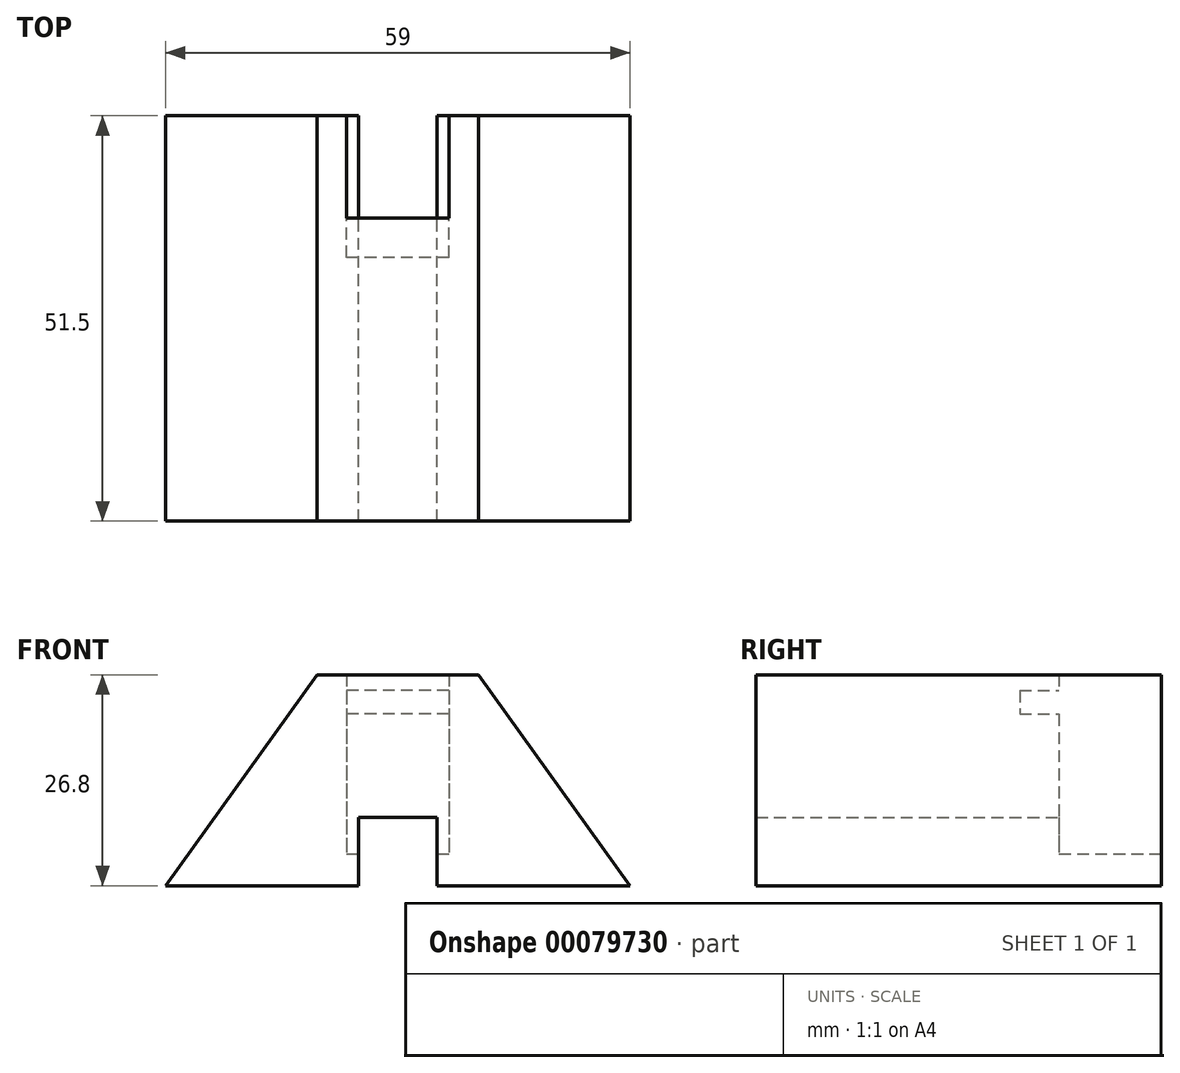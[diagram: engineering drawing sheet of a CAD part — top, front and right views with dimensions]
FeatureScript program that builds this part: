
annotation { "Feature Type Name" : "Feature", "Feature Type Description" : "" }
export const myFeature = defineFeature(function(context is Context, id is Id, definition is map)
    precondition{}
    {
        {
            var Q0;
            Q0=qCreatedBy(makeId("Top.planeOp"),FACE);
            var sketch = newSketch(context, id + "F0", { "sketchPlane" : qUnion([Q0])});
            skPoint(sketch, "E0.middle", {"position": v(0, 0) * mm});
            skLineSegment(sketch, "E1.bottom", {"start": v(-10.25, 25.75) * mm, "end": v(10.25, 25.75) * mm});
            skLineSegment(sketch, "E1.top", {"start": v(-10.25, -25.75) * mm, "end": v(10.25, -25.75) * mm});
            skLineSegment(sketch, "E1.left", {"start": v(-10.25, 25.75) * mm, "end": v(-10.25, -25.75) * mm});
            skLineSegment(sketch, "E1.right", {"start": v(10.25, 25.75) * mm, "end": v(10.25, -25.75) * mm});
            skLineSegment(sketch, "E2.bottom", {"start": v(-10.25, 25.75) * mm, "end": v(-29.5, 25.75) * mm});
            skLineSegment(sketch, "E2.top", {"start": v(-10.25, -25.75) * mm, "end": v(-29.5, -25.75) * mm});
            skLineSegment(sketch, "E2.right", {"start": v(-29.5, 25.75) * mm, "end": v(-29.5, -25.75) * mm});
            skLineSegment(sketch, "E3.bottom", {"start": v(10.25, 25.75) * mm, "end": v(29.5, 25.75) * mm});
            skLineSegment(sketch, "E3.top", {"start": v(10.25, -25.75) * mm, "end": v(29.5, -25.75) * mm});
            skLineSegment(sketch, "E3.right", {"start": v(29.5, 25.75) * mm, "end": v(29.5, -25.75) * mm});
            skSolve(sketch);
        }
        {
            var Q0;
            Q0 = qSketchRegion(id + "F0", true);
            extrude(context, id + "F1", {"entities" : qUnion([Q0]), "depth" : 26.8 * mm});
        }
        {
            var Q0;
            Q0=qCreatedBy(makeId("Top.planeOp"),FACE);
            var sketch = newSketch(context, id + "F2", { "sketchPlane" : qUnion([Q0])});
            skLineSegment(sketch, "E4.bottom", {"start": v(-6.5, 25.75) * mm, "end": v(6.5, 25.75) * mm});
            skLineSegment(sketch, "E4.top", {"start": v(-6.5, 12.75) * mm, "end": v(6.5, 12.75) * mm});
            skLineSegment(sketch, "E4.left", {"start": v(-6.5, 25.75) * mm, "end": v(-6.5, 12.75) * mm});
            skLineSegment(sketch, "E4.right", {"start": v(6.5, 25.75) * mm, "end": v(6.5, 12.75) * mm});
            skSolve(sketch);
        }
        {
            var Q0;
            Q0 = qSketchRegion(id + "F2", true);
            extrude(context, id + "F3", {"entities" : qUnion([Q0]), "operationType" : NewBodyOperationType.REMOVE, "depth" : 26.8 * mm});
        }
        {
            var Q0;
            Q0=makeQuery(id+"F0.imprint","IMPRINT",FACE,{"disambiguationData":[TD([[makeQuery(id+"F0.imprint","IMPRINT",EDGE,{"derivedFrom":sQuery(id+"F0.wireOp",EDGE,"E1.bottom")}),-1.0]])]});
            var sketch = newSketch(context, id + "F4", { "sketchPlane" : qUnion([Q0])});
            skLineSegment(sketch, "E5.bottom", {"start": v(-6.5, 12.75) * mm, "end": v(-5, 12.75) * mm});
            skLineSegment(sketch, "E5.top", {"start": v(-6.5, 25.75) * mm, "end": v(-5, 25.75) * mm});
            skLineSegment(sketch, "E5.left", {"start": v(-6.5, 12.75) * mm, "end": v(-6.5, 25.75) * mm});
            skLineSegment(sketch, "E5.right", {"start": v(-5, 12.75) * mm, "end": v(-5, 25.75) * mm});
            skLineSegment(sketch, "E6.bottom", {"start": v(5, 12.75) * mm, "end": v(6.5, 12.75) * mm});
            skLineSegment(sketch, "E6.top", {"start": v(5, 25.75) * mm, "end": v(6.5, 25.75) * mm});
            skLineSegment(sketch, "E6.left", {"start": v(5, 12.75) * mm, "end": v(5, 25.75) * mm});
            skLineSegment(sketch, "E6.right", {"start": v(6.5, 12.75) * mm, "end": v(6.5, 25.75) * mm});
            skSolve(sketch);
        }
        {
            var Q0;
            Q0 = qSketchRegion(id + "F4", true);
            extrude(context, id + "F5", {"entities" : qUnion([Q0]), "operationType" : NewBodyOperationType.ADD, "depth" : 4.05 * mm});
        }
        {
            var Q0;
            {var subQ0=sQuery(id+"F0.wireOp",EDGE,"E3.right");var subQ2=sQuery(id+"F0.wireOp",EDGE,"E3.bottom");var subQ5=sQuery(id+"F0.wireOp",EDGE,"E2.bottom");var subQ7=sQuery(id+"F0.wireOp",EDGE,"E1.bottom");Q0=makeQuery(id+"F5.boolean.opBoolean","MERGE",FACE,{"derivedFrom":[makeQuery(id+"F3.boolean.opBoolean","SPLIT",FACE,{"disambiguationData":[TD([makeQuery(id+"F1.opExtrude","SWEPT_FACE",FACE,{"disambiguationData":[OSD([subQ0])]})])],"derivedFrom":makeQuery(id+"F1.opExtrude","SWEPT_FACE",FACE,{"disambiguationData":[OSD([subQ7,subQ5,subQ2])]})}),makeQuery(id+"F5.opExtrude","SWEPT_FACE",FACE,{"disambiguationData":[OSD([sQuery(id+"F4.wireOp",EDGE,"E6.top")])]})]});}
            var sketch = newSketch(context, id + "F6", { "sketchPlane" : qUnion([Q0])});
            skLineSegment(sketch, "E7", {"start": v(29.5, 0) * mm, "end": v(10.24, 26.8) * mm});
            skLineSegment(sketch, "E8", {"start": v(10.24, 26.8) * mm, "end": v(29.5, 26.8) * mm});
            skLineSegment(sketch, "E9", {"start": v(29.5, 26.8) * mm, "end": v(29.5, 0) * mm});
            skLineSegment(sketch, "E10", {"start": v(-10.24, 26.8) * mm, "end": v(-29.5, 26.8) * mm});
            skLineSegment(sketch, "E11", {"start": v(-29.5, 26.8) * mm, "end": v(-29.5, 0) * mm});
            skLineSegment(sketch, "E12", {"start": v(-10.24, 26.8) * mm, "end": v(-29.5, 0) * mm});
            skSolve(sketch);
        }
        {
            var Q0;
            Q0 = qSketchRegion(id + "F6", true);
            extrude(context, id + "F7", {"entities" : qUnion([Q0]), "operationType" : NewBodyOperationType.REMOVE, "endBound" : BoundingType.THROUGH_ALL, "oppositeDirection" : true, "depth" : 25 * mm});
        }
        {
            var Q0;
            Q0=makeQuery(id+"F3.boolean.opBoolean","COPY",FACE,{"derivedFrom":makeQuery(id+"F3.opExtrude","SWEPT_FACE",FACE,{"disambiguationData":[OSD([sQuery(id+"F2.wireOp",EDGE,"E4.top")])]})});
            var sketch = newSketch(context, id + "F8", { "sketchPlane" : qUnion([Q0])});
            skLineSegment(sketch, "E13.bottom", {"start": v(-5, 8.67) * mm, "end": v(5, 8.67) * mm});
            skLineSegment(sketch, "E13.top", {"start": v(-5, 0) * mm, "end": v(5, 0) * mm});
            skLineSegment(sketch, "E13.left", {"start": v(-5, 8.67) * mm, "end": v(-5, 0) * mm});
            skLineSegment(sketch, "E13.right", {"start": v(5, 8.67) * mm, "end": v(5, 0) * mm});
            skSolve(sketch);
        }
        {
            var Q0;
            Q0 = qSketchRegion(id + "F8", true);
            extrude(context, id + "F9", {"entities" : qUnion([Q0]), "operationType" : NewBodyOperationType.REMOVE, "endBound" : BoundingType.THROUGH_ALL, "oppositeDirection" : true, "depth" : 25 * mm});
        }
        {
            var Q0;
            Q0=makeQuery(id+"F3.boolean.opBoolean","COPY",FACE,{"derivedFrom":makeQuery(id+"F3.opExtrude","SWEPT_FACE",FACE,{"disambiguationData":[OSD([sQuery(id+"F2.wireOp",EDGE,"E4.top")])]})});
            var sketch = newSketch(context, id + "F10", { "sketchPlane" : qUnion([Q0])});
            skLineSegment(sketch, "E14.bottom", {"start": v(-6.5, 24.8) * mm, "end": v(6.5, 24.8) * mm});
            skLineSegment(sketch, "E14.top", {"start": v(-6.5, 21.8) * mm, "end": v(6.5, 21.8) * mm});
            skLineSegment(sketch, "E14.left", {"start": v(-6.5, 24.8) * mm, "end": v(-6.5, 21.8) * mm});
            skLineSegment(sketch, "E14.right", {"start": v(6.5, 24.8) * mm, "end": v(6.5, 21.8) * mm});
            skSolve(sketch);
        }
        {
            var Q0;
            Q0 = qSketchRegion(id + "F10", true);
            extrude(context, id + "F11", {"entities" : qUnion([Q0]), "operationType" : NewBodyOperationType.REMOVE, "oppositeDirection" : true, "depth" : 5 * mm});
        }
    });
